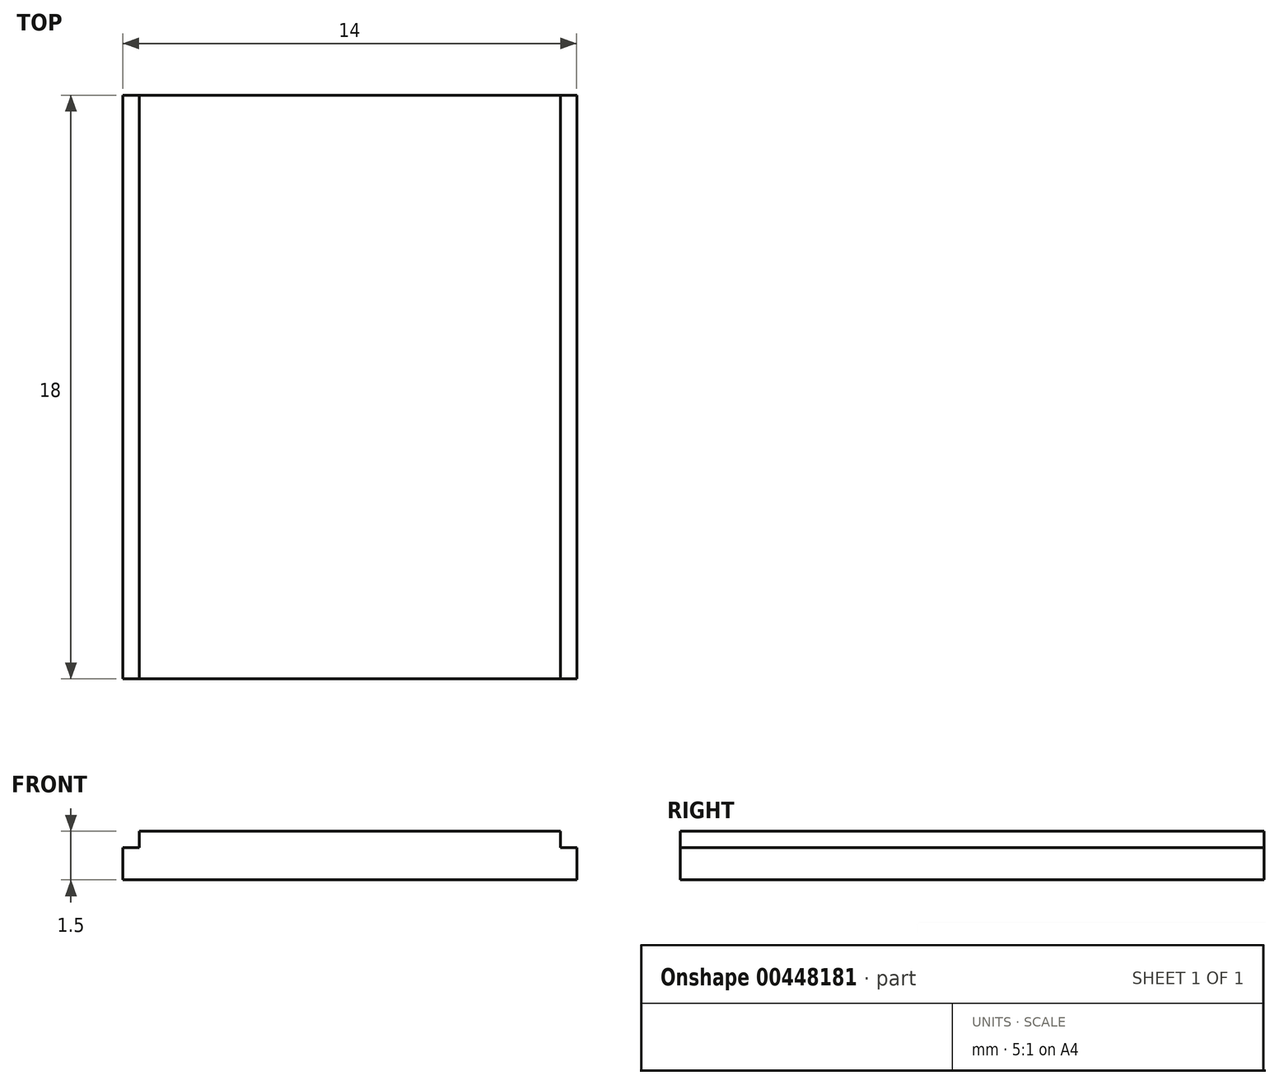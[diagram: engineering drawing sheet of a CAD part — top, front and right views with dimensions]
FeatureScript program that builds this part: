
annotation { "Feature Type Name" : "Feature", "Feature Type Description" : "" }
export const myFeature = defineFeature(function(context is Context, id is Id, definition is map)
    precondition{}
    {
        {
            var Q0;
            Q0=qCreatedBy(makeId("Top.planeOp"),FACE);
            var sketch = newSketch(context, id + "F0", { "sketchPlane" : qUnion([Q0])});
            skLineSegment(sketch, "E0", {"start": v(-15.59, 6.65) * mm, "end": v(-1.59, 6.65) * mm});
            skLineSegment(sketch, "E1", {"start": v(-1.59, 6.65) * mm, "end": v(-1.59, -11.35) * mm});
            skLineSegment(sketch, "E2", {"start": v(-1.59, -11.35) * mm, "end": v(-15.59, -11.35) * mm});
            skLineSegment(sketch, "E3", {"start": v(-15.59, -11.35) * mm, "end": v(-15.59, 6.65) * mm});
            skSolve(sketch);
        }
        {
            var Q0;
            Q0=makeQuery(id+"F0.imprint","IMPRINT",FACE,{"disambiguationData":[TD([[makeQuery(id+"F0.imprint","IMPRINT",EDGE,{"derivedFrom":sQuery(id+"F0.wireOp",EDGE,"E0")}),-1.0]])]});
            extrude(context, id + "F1", {"entities" : qUnion([Q0]), "depth" : 1 * mm});
        }
        {
            var Q0;
            Q0=makeQuery(id+"F1.opExtrude","CAP_FACE",FACE,{"disambiguationData":[OSD([sQuery(id+"F0.wireOp",EDGE,"E0"),sQuery(id+"F0.wireOp",EDGE,"E1"),sQuery(id+"F0.wireOp",EDGE,"E2"),sQuery(id+"F0.wireOp",EDGE,"E3")])],"isStart":false});
            var sketch = newSketch(context, id + "F2", { "sketchPlane" : qUnion([Q0])});
            skLineSegment(sketch, "E4", {"start": v(-15.09, -2.35) * mm, "end": v(-15.09, -11.35) * mm});
            skLineSegment(sketch, "E5", {"start": v(-15.09, -11.35) * mm, "end": v(-15.09, 6.65) * mm});
            skLineSegment(sketch, "E6", {"start": v(-2.09, -2.35) * mm, "end": v(-2.09, 6.65) * mm});
            skLineSegment(sketch, "E7", {"start": v(-2.09, 6.65) * mm, "end": v(-2.09, -11.35) * mm});
            skLineSegment(sketch, "E8", {"start": v(-2.09, -11.35) * mm, "end": v(-15.09, -11.35) * mm});
            skLineSegment(sketch, "E9", {"start": v(-15.09, 6.65) * mm, "end": v(-2.09, 6.65) * mm});
            skSolve(sketch);
        }
        {
            var Q0;
            {var subQ0=sQuery(id+"F2.wireOp",EDGE,"E8");Q0=makeQuery(id+"F2.imprint","IMPRINT",FACE,{"disambiguationData":[TD([[makeQuery(id+"F2.imprint","IMPRINT",EDGE,{"derivedFrom":subQ0}),-1.0]])]});}
            extrude(context, id + "F3", {"entities" : qUnion([Q0]), "operationType" : NewBodyOperationType.ADD, "depth" : .5 * mm});
        }
    });
